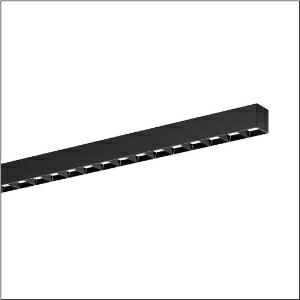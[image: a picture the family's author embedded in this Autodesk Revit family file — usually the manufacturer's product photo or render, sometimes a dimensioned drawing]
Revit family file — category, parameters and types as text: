
# Revit family: silica_21_51mx24dc4abb
name_source: partatom
category: Lighting Fixtures
units: mm (PartAtom-declared; Revit-internal decimal feet)

## family parameters
Cut with Voids When Loaded = No
Host = Face
Light Source = No
Part Type = Normal
Room Calculation Point = No
Round Connector Dimension = Use Diameter
Shared = No

## types (1)
- --- (1 x LED, 10800 lm, 73.7 W, 4000K)
    Apparent Load = 74 VA
    CIE Flux Codes = 74 94 99 100 100
    Color Rendering = 80
    Color Temperature = 4000K
    Default Elevation = 1800 mm
    Description = Silica 21, office luminaire, primary light control with darklight reflector, of PMMA, black, CAT 2 (L<= 3000cd/m²), light emission: direct distribution, primary light characteristic: asymmetric, installation type: surface-mounted, LED, rated luminous flux: 10.800lm, luminous efficacy: 147lm/W, light colour: 840, colour temperature: 4000K, control gear: DALI 2, with terminal, 3+2-pole, max. 2.5mm², mains connection: 220..240V, AC, 50/60Hz, rated input power: 73.7W, luminaire housing, of aluminium, matt jet black (RAL 9005), length: 3.004mm, width: 53mm, height: 53mm, protection rating (complete): IP20, insulation class (complete): insulation class I (protective earthing), certification: CE, permissible operating ambient temperature: 0..+35°C, standard: EN 50419, packaging unit: 1 piece
    Height = 53 mm
    Lamp = 1 x LED
    Lamp Light Flux = 10800 lm
    Lamp Power = 73.7 W
    Lamp count = 1
    Length = 3004 mm
    Luminous efficacy = 147 lm/W
    Manufacturer = Siteco
    ModVariant = No
    Model = 51MX24DC4ABB
    Mounting Place = Ceiling
    Mounting Type = Surface mounted
    Number of Poles = 1
    OnlyDefault = Yes
    Power Factor = 1
    Product Name = Silica 21
    Product group = office luminaire | ceiling mounted
    ProductGroupID = 301
    Protection Class = Protection class I
    Protection Degree = IP 20
    RLX_Detail_Level = 1
    RLX_Emergency_Light_Flux = 0 lm
    RLX_Emergency_Type = 0
    RLX_Emergency_Type_DB = No
    RlxData = <blob elided: 64761 chars, md5=8329d5ef>
    Socket = socket
    Standby Power = 0 W
    System Light Flux = 10800 lm
    System Power = 74 W
    Type Comments = factory setting: luminous flux: 100 % | dim-lin: 254 | 418 mA
    Type Image = l_1335908.jpg
    URL = http://relux.com
    VarID = @adj_124589
    Voltage = 0 V
    Weight = 0.00 kg
    Width = 53 mm

## geometry (parser evidence)
native form markers: Blend x4, Sweep x11
no freeform markers — native parametric forms only
